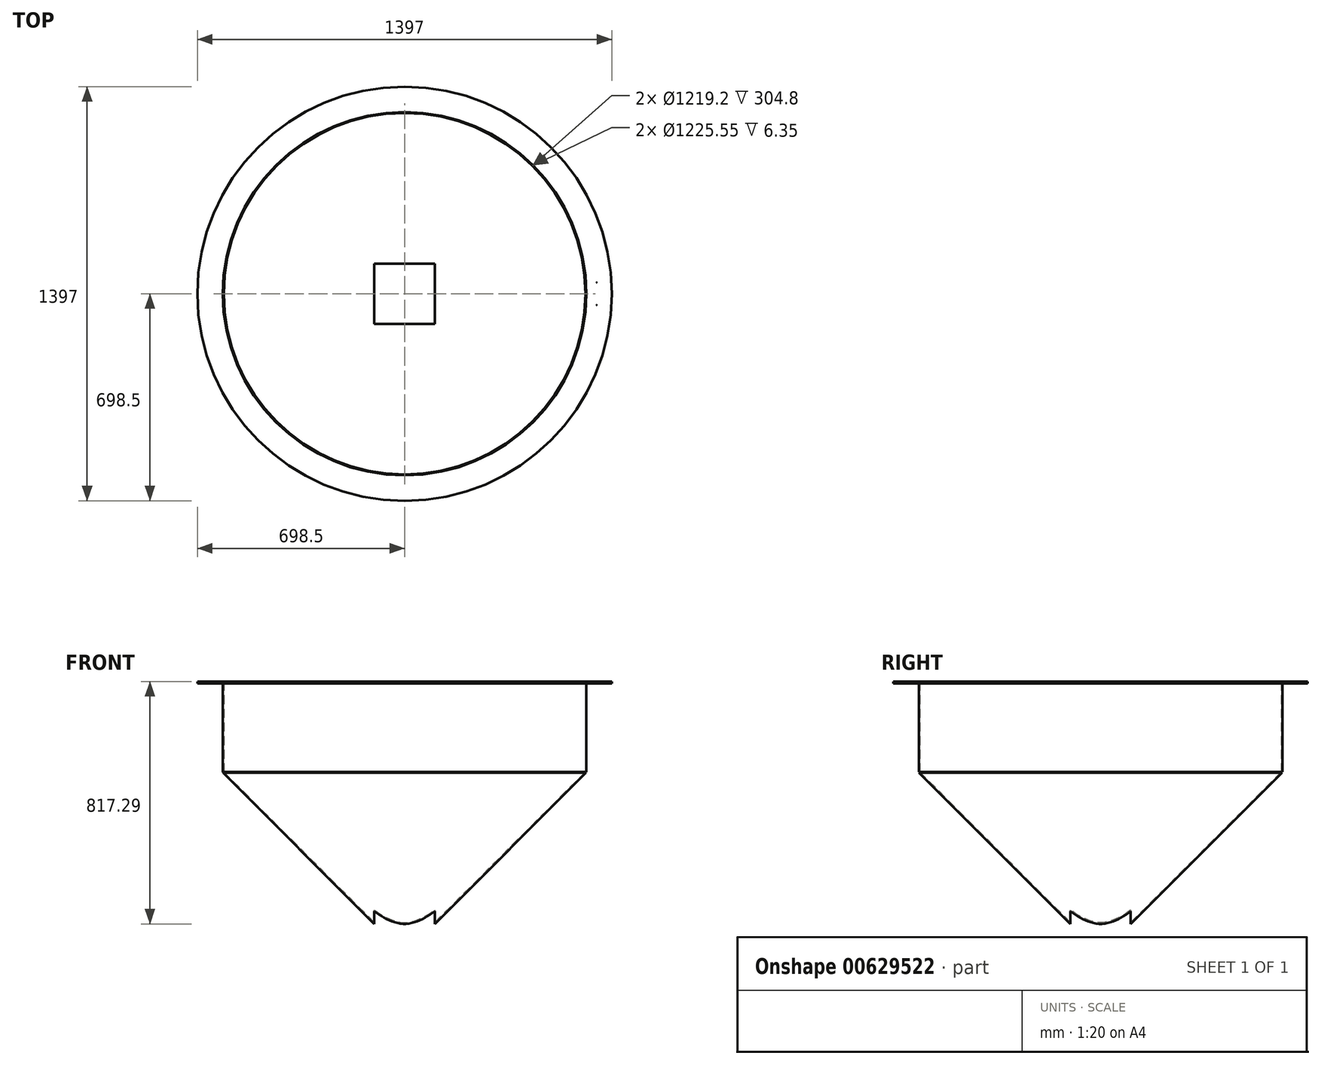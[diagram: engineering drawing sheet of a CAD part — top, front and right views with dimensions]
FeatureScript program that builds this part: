
annotation { "Feature Type Name" : "Feature", "Feature Type Description" : "" }
export const myFeature = defineFeature(function(context is Context, id is Id, definition is map)
    precondition{}
    {
        {
            var Q0;
            Q0=qCreatedBy(makeId("Front.planeOp"),FACE);
            var sketch = newSketch(context, id + "F0", { "sketchPlane" : qUnion([Q0])});
            skLineSegment(sketch, "E0", {"start": v(0, 0) * mm, "end": v(609.6, 609.6) * mm});
            skLineSegment(sketch, "E1", {"start": v(609.6, 609.6) * mm, "end": v(611.85, 607.35) * mm});
            skLineSegment(sketch, "E2", {"start": v(611.85, 607.35) * mm, "end": v(2.25, -2.25) * mm});
            skLineSegment(sketch, "E3", {"start": v(2.25, -2.25) * mm, "end": v(0, 0) * mm});
            skLineSegment(sketch, "E4", {"start": v(0, 0) * mm, "end": v(0, 47.15) * mm, "construction": true});
            skLineSegment(sketch, "E5", {"start": v(2.25, -2.25) * mm, "end": v(2.25, 2.25) * mm});
            skSolve(sketch);
        }
        {
            var Q0;
            {var subQ0=sQuery(id+"F0.wireOp",EDGE,"E1");Q0=makeQuery(id+"F0.imprint","IMPRINT",FACE,{"disambiguationData":[TD([[makeQuery(id+"F0.imprint","IMPRINT",EDGE,{"derivedFrom":subQ0}),-1.0]])]});}
            var Q1;
            Q1=sQuery(id+"F0.wireOp",EDGE,"E4");
            revolve(context, id + "F1", {"entities" : qUnion([Q0]), "axis" : qUnion([Q1]), "revolveType" : RevolveType.FULL});
        }
        {
            var Q0;
            Q0=qCreatedBy(makeId("Top.planeOp"),FACE);
            var sketch = newSketch(context, id + "F2", { "sketchPlane" : qUnion([Q0])});
            skLineSegment(sketch, "E6.bottom", {"start": v(101.6, -101.6) * mm, "end": v(-101.6, -101.6) * mm});
            skLineSegment(sketch, "E6.top", {"start": v(101.6, 101.6) * mm, "end": v(-101.6, 101.6) * mm});
            skLineSegment(sketch, "E6.left", {"start": v(101.6, -101.6) * mm, "end": v(101.6, 101.6) * mm});
            skLineSegment(sketch, "E6.right", {"start": v(-101.6, -101.6) * mm, "end": v(-101.6, 101.6) * mm});
            skPoint(sketch, "E6.middle", {"position": v(0, 0) * mm});
            skSolve(sketch);
        }
        {
            var Q0;
            Q0=makeQuery(id+"F2.imprint","IMPRINT",FACE,{"disambiguationData":[TD([[makeQuery(id+"F2.imprint","IMPRINT",EDGE,{"derivedFrom":sQuery(id+"F2.wireOp",EDGE,"E6.bottom")}),-1.0]])]});
            extrude(context, id + "F3", {"entities" : qUnion([Q0]), "operationType" : NewBodyOperationType.REMOVE, "endBound" : BoundingType.THROUGH_ALL, "oppositeDirection" : true, "depth" : 25.4 * mm, "hasSecondDirection" : true, "secondDirectionBound" : BoundingType.THROUGH_ALL, "secondDirectionOppositeDirection" : false, "secondDirectionDepth" : 25.4 * mm});
        }
        {
            var Q0;
            Q0=qCreatedBy(makeId("Front.planeOp"),FACE);
            var sketch = newSketch(context, id + "F4", { "sketchPlane" : qUnion([Q0])});
            skLineSegment(sketch, "E7.bottom", {"start": v(609.6, 609.6) * mm, "end": v(612.77, 609.6) * mm});
            skLineSegment(sketch, "E7.top", {"start": v(609.6, 914.4) * mm, "end": v(612.77, 914.4) * mm});
            skLineSegment(sketch, "E7.left", {"start": v(609.6, 609.6) * mm, "end": v(609.6, 914.4) * mm});
            skLineSegment(sketch, "E7.right", {"start": v(612.77, 609.6) * mm, "end": v(612.77, 914.4) * mm});
            skSolve(sketch);
        }
        {
            var Q0;
            Q0=makeQuery(id+"F4.imprint","IMPRINT",FACE,{"disambiguationData":[TD([[makeQuery(id+"F4.imprint","IMPRINT",EDGE,{"derivedFrom":sQuery(id+"F4.wireOp",EDGE,"E7.bottom")}),1.0]])]});
            var Q1;
            Q1=sQuery(id+"F0.wireOp",EDGE,"E4");
            revolve(context, id + "F5", {"entities" : qUnion([Q0]), "axis" : qUnion([Q1]), "revolveType" : RevolveType.FULL});
        }
        {
            var Q0;
            Q0=qCreatedBy(makeId("Front.planeOp"),FACE);
            var sketch = newSketch(context, id + "F6", { "sketchPlane" : qUnion([Q0])});
            skLineSegment(sketch, "E8.bottom", {"start": v(612.77, 914.4) * mm, "end": v(698.5, 914.4) * mm});
            skLineSegment(sketch, "E8.top", {"start": v(612.77, 908.05) * mm, "end": v(698.5, 908.05) * mm});
            skLineSegment(sketch, "E8.left", {"start": v(612.77, 914.4) * mm, "end": v(612.77, 908.05) * mm});
            skLineSegment(sketch, "E8.right", {"start": v(698.5, 914.4) * mm, "end": v(698.5, 908.05) * mm});
            skSolve(sketch);
        }
        {
            var Q0;
            Q0=makeQuery(id+"F6.imprint","IMPRINT",FACE,{"disambiguationData":[TD([[makeQuery(id+"F6.imprint","IMPRINT",EDGE,{"derivedFrom":sQuery(id+"F6.wireOp",EDGE,"E8.bottom")}),-1.0]])]});
            var Q1;
            Q1=sQuery(id+"F0.wireOp",EDGE,"E4");
            revolve(context, id + "F7", {"entities" : qUnion([Q0]), "axis" : qUnion([Q1]), "revolveType" : RevolveType.FULL});
        }
        {
            var Q0;
            Q0=makeQuery(id+"F7.opRevolve","SWEPT_FACE",FACE,{"disambiguationData":[OSD([sQuery(id+"F6.wireOp",EDGE,"E8.bottom")])]});
            var sketch = newSketch(context, id + "F8", { "sketchPlane" : qUnion([Q0])});
            skLineSegment(sketch, "E9", {"start": v(647.7, 38.1) * mm, "end": v(647.7, -38.1) * mm, "construction": true});
            skLineSegment(sketch, "E10", {"start": v(0, 0) * mm, "end": v(647.7, 0) * mm, "construction": true});
            skSolve(sketch);
        }
        {
            var Q0;
            Q0=sQuery(id+"F8.wireOp",VERTEX,"E9.start");
            var Q1;
            Q1=sQuery(id+"F8.wireOp",VERTEX,"E9.end");
            var Q2;
            Q2=makeQuery(id+"F7.opRevolve","SWEPT_BODY",BODY,{"disambiguationData":[OSD([sQuery(id+"F6.wireOp",EDGE,"E8.bottom"),sQuery(id+"F6.wireOp",EDGE,"E8.top"),sQuery(id+"F6.wireOp",EDGE,"E8.left"),sQuery(id+"F6.wireOp",EDGE,"E8.right")])]});
            hole(context, id + "F9", {"style" : HoleStyle.SIMPLE, "endStyle" : HoleEndStyle.THROUGH, "standardTappedOrClearance" : lookupTablePath({ "standard" : "ANSI", "size" : "13/32 (0.4)", "type" : "Drilled" }), "standardBlindInLast" : lookupTablePath({ "standard" : "ANSI", "size" : "13/32", "type" : "Drilled" }), "holeDiameter" : 13 / 812.8 * mm, "isTappedThrough" : true, "tappedDepth" : 12.7 * mm, "tapClearance" : 3, "locations" : qUnion([Q0, Q1]), "scope" : qUnion([Q2])});
        }
    });
